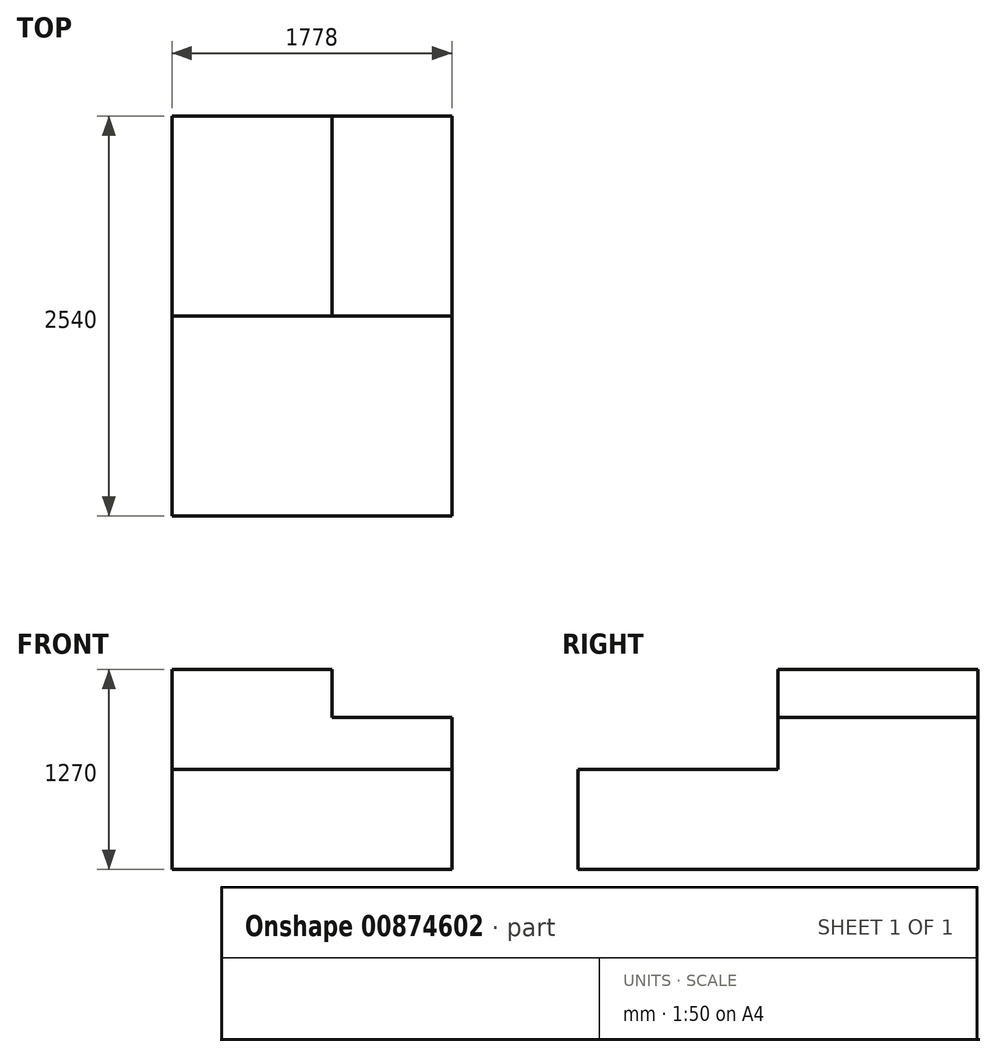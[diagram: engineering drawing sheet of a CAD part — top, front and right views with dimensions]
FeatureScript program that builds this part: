
annotation { "Feature Type Name" : "Feature", "Feature Type Description" : "" }
export const myFeature = defineFeature(function(context is Context, id is Id, definition is map)
    precondition{}
    {
        {
            var Q0;
            Q0=qCreatedBy(makeId("Top.planeOp"),FACE);
            var sketch = newSketch(context, id + "F0", { "sketchPlane" : qUnion([Q0])});
            skLineSegment(sketch, "E0.bottom", {"start": v(0, 0) * mm, "end": v(1778, 0) * mm});
            skLineSegment(sketch, "E0.top", {"start": v(0, 2540) * mm, "end": v(1778, 2540) * mm});
            skLineSegment(sketch, "E0.left", {"start": v(0, 0) * mm, "end": v(0, 2540) * mm});
            skLineSegment(sketch, "E0.right", {"start": v(1778, 0) * mm, "end": v(1778, 2540) * mm});
            skSolve(sketch);
        }
        {
            var Q0;
            Q0=makeQuery(id+"F0.imprint","IMPRINT",FACE,{"disambiguationData":[TD([[makeQuery(id+"F0.imprint","IMPRINT",EDGE,{"derivedFrom":sQuery(id+"F0.wireOp",EDGE,"E0.bottom")}),1.0]])]});
            extrude(context, id + "F1", {"entities" : qUnion([Q0]), "depth" : 1270 * mm, "offsetDistance" : 25.4 * mm});
        }
        {
            var Q0;
            Q0=makeQuery(id+"F1.opExtrude","CAP_FACE",FACE,{"disambiguationData":[OSD([sQuery(id+"F0.wireOp",EDGE,"E0.bottom"),sQuery(id+"F0.wireOp",EDGE,"E0.top"),sQuery(id+"F0.wireOp",EDGE,"E0.left"),sQuery(id+"F0.wireOp",EDGE,"E0.right")])],"isStart":false});
            var sketch = newSketch(context, id + "F2", { "sketchPlane" : qUnion([Q0])});
            skLineSegment(sketch, "E1.bottom", {"start": v(0, 0) * mm, "end": v(1778, 0) * mm});
            skLineSegment(sketch, "E1.top", {"start": v(0, 1270) * mm, "end": v(1778, 1270) * mm});
            skLineSegment(sketch, "E1.left", {"start": v(0, 0) * mm, "end": v(0, 1270) * mm});
            skLineSegment(sketch, "E1.right", {"start": v(1778, 0) * mm, "end": v(1778, 1270) * mm});
            skSolve(sketch);
        }
        {
            var Q0;
            Q0=makeQuery(id+"F2.imprint","IMPRINT",FACE,{"disambiguationData":[TD([[makeQuery(id+"F2.imprint","IMPRINT",EDGE,{"derivedFrom":sQuery(id+"F2.wireOp",EDGE,"E1.bottom")}),1.0]])]});
            extrude(context, id + "F3", {"entities" : qUnion([Q0]), "operationType" : NewBodyOperationType.REMOVE, "oppositeDirection" : true, "depth" : 635 * mm, "offsetDistance" : 25.4 * mm});
        }
        {
            var Q0;
            Q0=makeQuery(id+"F1.opExtrude","CAP_FACE",FACE,{"disambiguationData":[OSD([sQuery(id+"F0.wireOp",EDGE,"E0.bottom"),sQuery(id+"F0.wireOp",EDGE,"E0.top"),sQuery(id+"F0.wireOp",EDGE,"E0.left"),sQuery(id+"F0.wireOp",EDGE,"E0.right")])],"isStart":false});
            var sketch = newSketch(context, id + "F4", { "sketchPlane" : qUnion([Q0])});
            skLineSegment(sketch, "E2.bottom", {"start": v(1778, 2540) * mm, "end": v(1016, 2540) * mm});
            skLineSegment(sketch, "E2.top", {"start": v(1778, 1270) * mm, "end": v(1016, 1270) * mm});
            skLineSegment(sketch, "E2.left", {"start": v(1778, 2540) * mm, "end": v(1778, 1270) * mm});
            skLineSegment(sketch, "E2.right", {"start": v(1016, 2540) * mm, "end": v(1016, 1270) * mm});
            skSolve(sketch);
        }
        {
            var Q0;
            Q0=makeQuery(id+"F4.imprint","IMPRINT",FACE,{"disambiguationData":[TD([[makeQuery(id+"F4.imprint","IMPRINT",EDGE,{"derivedFrom":sQuery(id+"F4.wireOp",EDGE,"E2.bottom")}),-1.0]])]});
            extrude(context, id + "F5", {"entities" : qUnion([Q0]), "operationType" : NewBodyOperationType.REMOVE, "oppositeDirection" : true, "depth" : 304.8 * mm, "offsetDistance" : 25.4 * mm});
        }
    });
